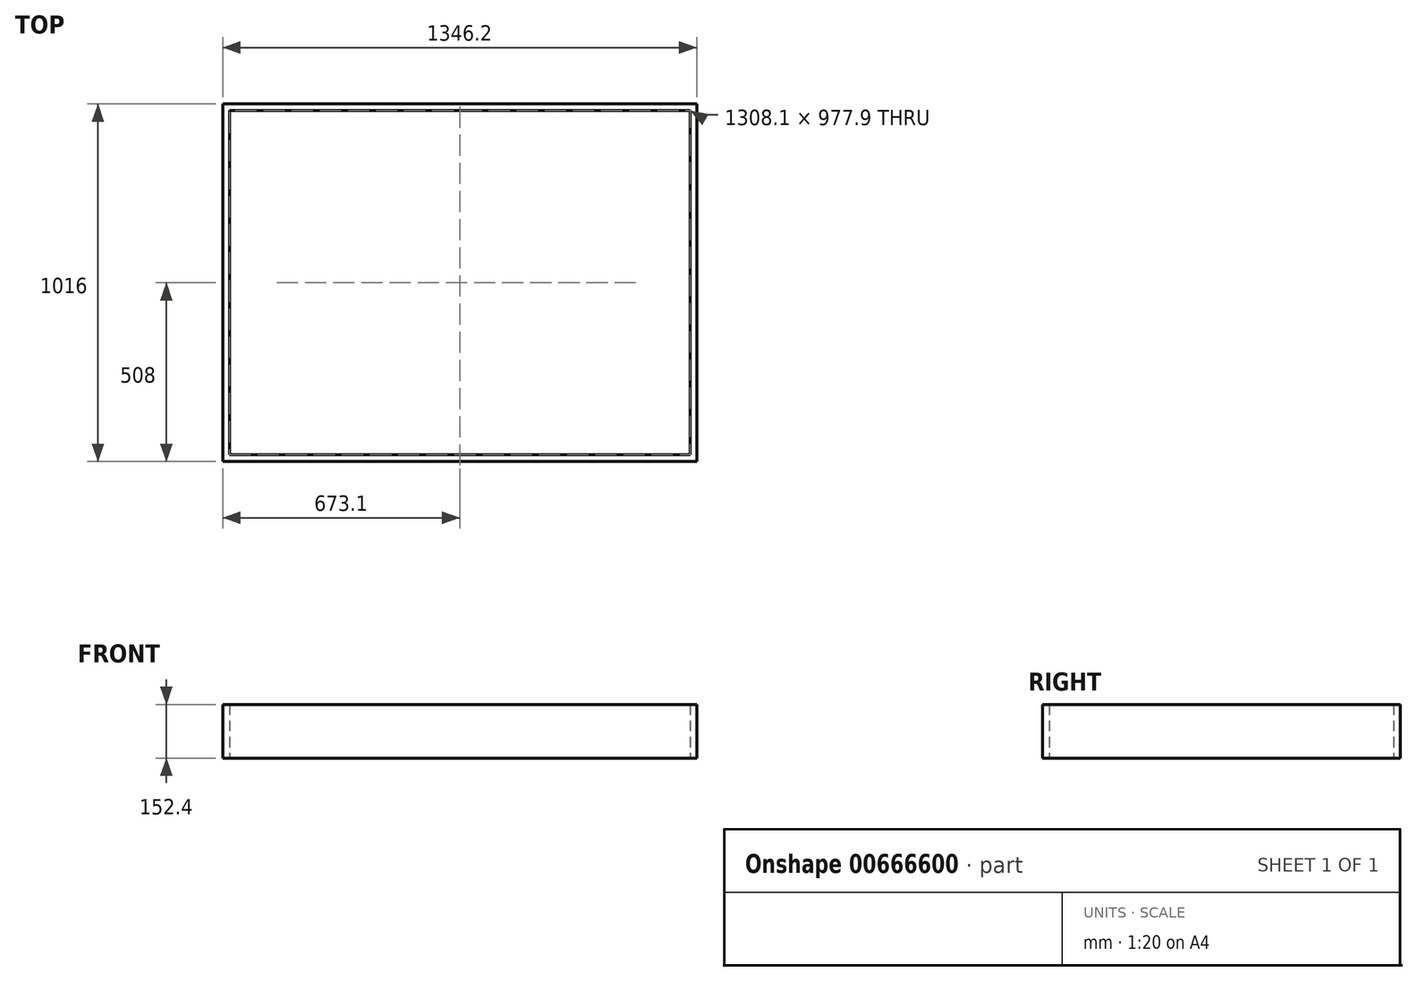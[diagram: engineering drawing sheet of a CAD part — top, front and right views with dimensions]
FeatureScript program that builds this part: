
annotation { "Feature Type Name" : "Feature", "Feature Type Description" : "" }
export const myFeature = defineFeature(function(context is Context, id is Id, definition is map)
    precondition{}
    {
        {
            var Q0;
            Q0=qCreatedBy(makeId("Top.planeOp"),FACE);
            var sketch = newSketch(context, id + "F0", { "sketchPlane" : qUnion([Q0])});
            skLineSegment(sketch, "E0.bottom", {"start": v(-673.1, 508) * mm, "end": v(673.1, 508) * mm});
            skLineSegment(sketch, "E0.top", {"start": v(-673.1, -508) * mm, "end": v(673.1, -508) * mm});
            skLineSegment(sketch, "E0.left", {"start": v(-673.1, 508) * mm, "end": v(-673.1, -508) * mm});
            skLineSegment(sketch, "E0.right", {"start": v(673.1, 508) * mm, "end": v(673.1, -508) * mm});
            skPoint(sketch, "E0.middle", {"position": v(0, 0) * mm});
            skLineSegment(sketch, "E1.bottom", {"start": v(-654.05, 488.95) * mm, "end": v(654.05, 488.95) * mm});
            skLineSegment(sketch, "E1.top", {"start": v(-654.05, -488.95) * mm, "end": v(654.05, -488.95) * mm});
            skLineSegment(sketch, "E1.left", {"start": v(-654.05, 488.95) * mm, "end": v(-654.05, -488.95) * mm});
            skLineSegment(sketch, "E1.right", {"start": v(654.05, 488.95) * mm, "end": v(654.05, -488.95) * mm});
            skSolve(sketch);
        }
        {
            var Q0;
            Q0=makeQuery(id+"F0.imprint","IMPRINT",FACE,{"disambiguationData":[TD([[makeQuery(id+"F0.imprint","IMPRINT",EDGE,{"derivedFrom":sQuery(id+"F0.wireOp",EDGE,"E0.bottom")}),-1.0]])]});
            extrude(context, id + "F1", {"entities" : qUnion([Q0]), "depth" : 152.4 * mm, "offsetDistance" : 25.4 * mm});
        }
    });
